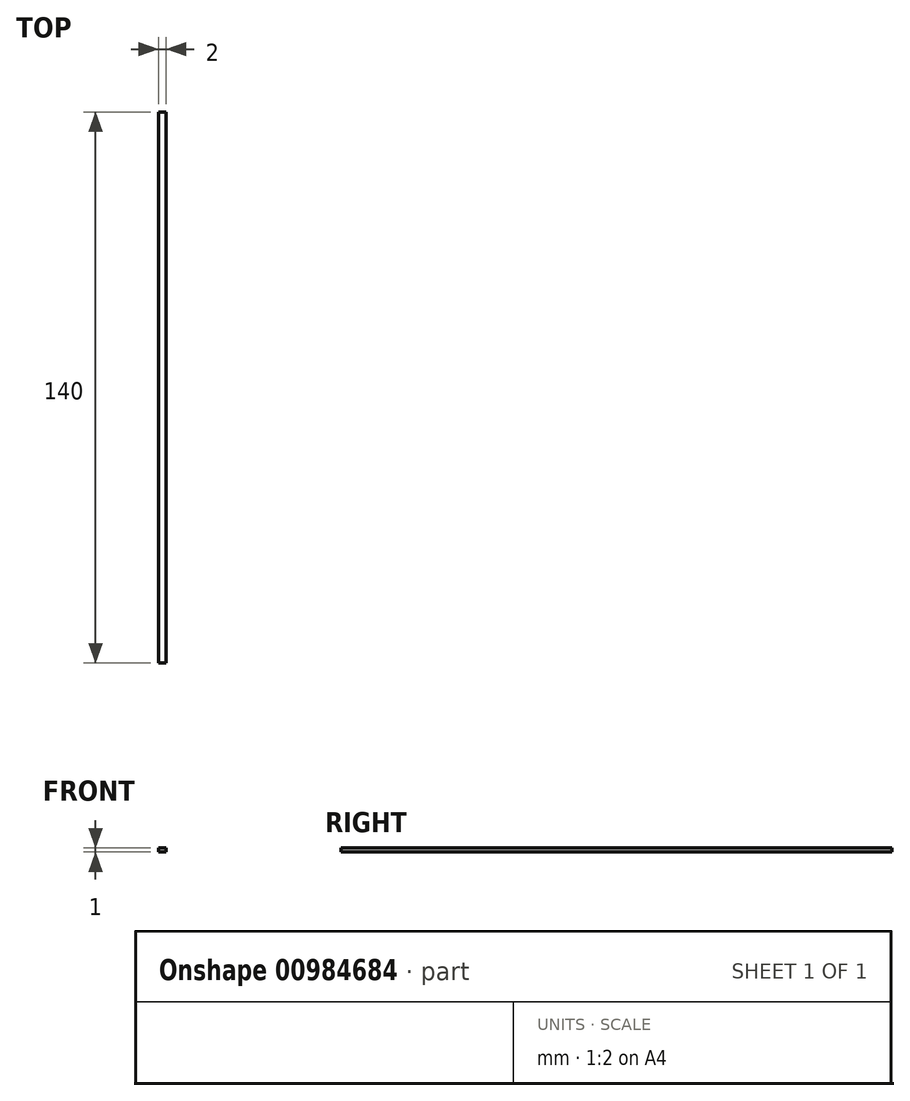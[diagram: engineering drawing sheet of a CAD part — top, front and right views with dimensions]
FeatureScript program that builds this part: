
annotation { "Feature Type Name" : "Feature", "Feature Type Description" : "" }
export const myFeature = defineFeature(function(context is Context, id is Id, definition is map)
    precondition{}
    {
        {
            var Q0;
            Q0=qCreatedBy(makeId("Front.planeOp"),FACE);
            var sketch = newSketch(context, id + "F0", { "sketchPlane" : qUnion([Q0])});
            skLineSegment(sketch, "E0.bottom", {"start": v(-1, 1) * mm, "end": v(1, 1) * mm});
            skLineSegment(sketch, "E0.top", {"start": v(-1, 0) * mm, "end": v(1, 0) * mm});
            skLineSegment(sketch, "E0.left", {"start": v(-1, 1) * mm, "end": v(-1, 0) * mm});
            skLineSegment(sketch, "E0.right", {"start": v(1, 1) * mm, "end": v(1, 0) * mm});
            skSolve(sketch);
        }
        {
            var Q0;
            Q0=makeQuery(id+"F0.imprint","IMPRINT",FACE,{"disambiguationData":[TD([[makeQuery(id+"F0.imprint","IMPRINT",EDGE,{"derivedFrom":sQuery(id+"F0.wireOp",EDGE,"E0.bottom")}),-1.0]])]});
            extrude(context, id + "F1", {"entities" : qUnion([Q0]), "endBound" : BoundingType.SYMMETRIC, "depth" : 140 * mm, "offsetDistance" : 25 * mm});
        }
    });
